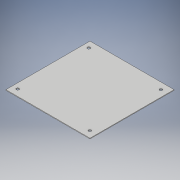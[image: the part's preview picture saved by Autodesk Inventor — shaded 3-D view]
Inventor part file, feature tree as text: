
AUTODESK INVENTOR PART (.ipt)
format: ipt  version: 2018 (Build 220112000, 112)  size: 104,960 bytes
history: native  units: in
note: dims shown in document units (in); Inventor stores cm internally (conversion verified against a paired STEP export)
features: extrude x2, sketch x2
ambient origin geometry x8: Origin, YZ Plane, XZ Plane, XY Plane, X Axis, Y Axis, Z Axis, Center Point
bodies: Solid1 (feature_tree)
feature tree (4):
  extrude  "Extrusion1"  Depth=3.937in
  extrude  "Extrusion2"  Depth=0.031in
  sketch  "Sketch1"  dims[d0=3.937in d1=3.937in]
  sketch  "Sketch2"  dims[d2=0.031in d3=0.0in d4=0.1285in d5=0.1285in d6=0.1285in d7=0.1285in d8=0.0in d9=0.0in]
